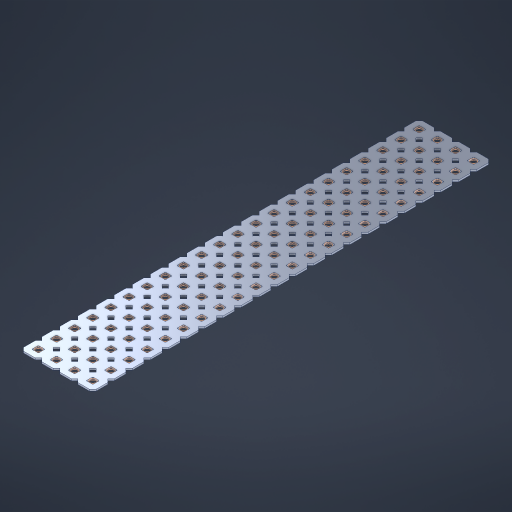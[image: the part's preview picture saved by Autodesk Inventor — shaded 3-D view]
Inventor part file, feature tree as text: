
AUTODESK INVENTOR PART (.ipt)
format: ipt  version: 2023 (Build 270158000, 158)  size: 1,275,392 bytes
history: native  units: in
note: dims shown in document units (in); Inventor stores cm internally (conversion verified against a paired STEP export)
features: other x89, extrude x87, sketch x2, pattern_linear x1
ambient origin geometry x8: Origin, YZ Plane, XZ Plane, XY Plane, X Axis, Y Axis, Z Axis, Center Point
bodies: Solid1 (feature_tree), Body (feature_tree)
feature tree (179):
  pattern_linear  "Rectangular Pattern1"  Spacing1=0.09in  [1 undecoded]
  sketch  "Sketch1"  dims[d1=0.5in]
  sketch  "Sketch2"  dims[d2=0.182in d3=0.09in d4=0.09in d5=0.09in d6=0.09in d7=0.09in d8=0.09in d9=0.09in d10=0.09in d11=0.02in d13=0.0in d14=0.172in d15=0.0625in d16=0.0in d19=0.5in d22=0.5in]
  other  "Srf1"
  other  "Srf126"
  other  "Srf127"
  other  "Srf128"
  other  "Srf129"
  other  "Srf130"
  other  "Srf131"
  other  "Srf250"
  other  "Srf251"
  other  "Srf252"
  other  "Srf253"
  other  "Srf254"
  other  "Srf255"
  other  "Srf256"
  other  "Srf257"
  other  "Srf258"
  other  "Srf259"
  other  "Srf260"
  other  "Srf261"
  other  "Srf262"
  other  "Srf263"
  other  "Srf264"
  other  "Srf268"
  other  "Srf269"
  other  "Srf270"
  other  "Srf271"
  other  "Srf272"
  other  "Srf273"
  other  "Srf274"
  other  "Srf275"
  other  "Srf276"
  other  "Srf277"
  other  "Srf278"
  other  "Srf279"
  other  "Srf280"
  other  "Srf281"
  other  "Srf282"
  other  "Srf283"
  other  "Srf284"
  other  "Srf285"
  other  "Srf286"
  other  "Srf287"
  other  "Srf288"
  other  "Srf289"
  other  "Srf293"
  other  "Srf294"
  other  "Srf295"
  other  "Srf296"
  other  "Srf297"
  other  "Srf298"
  other  "Srf299"
  other  "Srf300"
  other  "Srf301"
  other  "Srf302"
  other  "Srf303"
  other  "Srf304"
  other  "Srf305"
  other  "Srf306"
  other  "Srf307"
  other  "Srf308"
  other  "Srf309"
  other  "Srf310"
  other  "Srf311"
  other  "Srf312"
  other  "Srf313"
  other  "Srf314"
  other  "Srf318"
  other  "Srf319"
  other  "Srf320"
  other  "Srf321"
  other  "Srf322"
  other  "Srf323"
  other  "Srf324"
  other  "Srf325"
  other  "Srf326"
  other  "Srf327"
  other  "Srf328"
  other  "Srf329"
  other  "Srf330"
  other  "Srf331"
  other  "Srf332"
  other  "Srf333"
  other  "Srf334"
  other  "Srf335"
  other  "Srf336"
  other  "Srf337"
  other  "Srf338"
  other  "Srf339"
  other  "Circle"
  extrude  "ExtrusionSrf126"  Depth=0.09in
  extrude  "ExtrusionSrf127"  Depth=0.09in
  extrude  "ExtrusionSrf128"  Depth=0.09in
  extrude  "ExtrusionSrf129"  Depth=0.09in
  extrude  "ExtrusionSrf130"  Depth=0.09in
  extrude  "ExtrusionSrf131"  Depth=0.09in
  extrude  "ExtrusionSrf250"  Depth=0.09in
  extrude  "ExtrusionSrf251"  Depth=0.02in
  extrude  "ExtrusionSrf252"  TaperAngle=0.0deg  [1 undecoded]
  extrude  "ExtrusionSrf253"  Depth=0.5in
  extrude  "ExtrusionSrf254"  Depth=0.5in TaperAngle=0.0deg
  extrude  "ExtrusionSrf255"  Depth=0.5in
  extrude  "ExtrusionSrf256"  Depth=0.5in
  extrude  "ExtrusionSrf257"  [1 undecoded]
  extrude  "ExtrusionSrf258"  [1 undecoded]
  extrude  "ExtrusionSrf259"  [1 undecoded]
  extrude  "ExtrusionSrf260"  [1 undecoded]
  extrude  "ExtrusionSrf261"  [1 undecoded]
  extrude  "ExtrusionSrf262"  [1 undecoded]
  extrude  "ExtrusionSrf263"  [1 undecoded]
  extrude  "ExtrusionSrf264"  [1 undecoded]
  extrude  "ExtrusionSrf268"  [1 undecoded]
  extrude  "ExtrusionSrf269"  [1 undecoded]
  extrude  "ExtrusionSrf270"  [1 undecoded]
  extrude  "ExtrusionSrf271"  [1 undecoded]
  extrude  "ExtrusionSrf272"  [1 undecoded]
  extrude  "ExtrusionSrf273"  [1 undecoded]
  extrude  "ExtrusionSrf274"  [1 undecoded]
  extrude  "ExtrusionSrf275"  [1 undecoded]
  extrude  "ExtrusionSrf276"  [1 undecoded]
  extrude  "ExtrusionSrf277"  [1 undecoded]
  extrude  "ExtrusionSrf278"  [1 undecoded]
  extrude  "ExtrusionSrf279"  [1 undecoded]
  extrude  "ExtrusionSrf280"  [1 undecoded]
  extrude  "ExtrusionSrf281"  [1 undecoded]
  extrude  "ExtrusionSrf282"  [1 undecoded]
  extrude  "ExtrusionSrf283"  [1 undecoded]
  extrude  "ExtrusionSrf284"  [1 undecoded]
  extrude  "ExtrusionSrf285"  [1 undecoded]
  extrude  "ExtrusionSrf286"  [1 undecoded]
  extrude  "ExtrusionSrf287"  [1 undecoded]
  extrude  "ExtrusionSrf288"  [1 undecoded]
  extrude  "ExtrusionSrf289"  [1 undecoded]
  extrude  "ExtrusionSrf293"  [1 undecoded]
  extrude  "ExtrusionSrf294"  [1 undecoded]
  extrude  "ExtrusionSrf295"  [1 undecoded]
  extrude  "ExtrusionSrf296"  [1 undecoded]
  extrude  "ExtrusionSrf297"  [1 undecoded]
  extrude  "ExtrusionSrf298"  [1 undecoded]
  extrude  "ExtrusionSrf299"  [1 undecoded]
  extrude  "ExtrusionSrf300"  [1 undecoded]
  extrude  "ExtrusionSrf301"  [1 undecoded]
  extrude  "ExtrusionSrf302"  [1 undecoded]
  extrude  "ExtrusionSrf303"  [1 undecoded]
  extrude  "ExtrusionSrf304"  [1 undecoded]
  extrude  "ExtrusionSrf305"  [1 undecoded]
  extrude  "ExtrusionSrf306"  [1 undecoded]
  extrude  "ExtrusionSrf307"  [1 undecoded]
  extrude  "ExtrusionSrf308"  [1 undecoded]
  extrude  "ExtrusionSrf309"  [1 undecoded]
  extrude  "ExtrusionSrf310"  [1 undecoded]
  extrude  "ExtrusionSrf311"  [1 undecoded]
  extrude  "ExtrusionSrf312"  [1 undecoded]
  extrude  "ExtrusionSrf313"  [1 undecoded]
  extrude  "ExtrusionSrf314"  [1 undecoded]
  extrude  "ExtrusionSrf318"  [1 undecoded]
  extrude  "ExtrusionSrf319"  [1 undecoded]
  extrude  "ExtrusionSrf320"  [1 undecoded]
  extrude  "ExtrusionSrf321"  [1 undecoded]
  extrude  "ExtrusionSrf322"  [1 undecoded]
  extrude  "ExtrusionSrf323"  [1 undecoded]
  extrude  "ExtrusionSrf324"  [1 undecoded]
  extrude  "ExtrusionSrf325"  [1 undecoded]
  extrude  "ExtrusionSrf326"  [1 undecoded]
  extrude  "ExtrusionSrf327"  [1 undecoded]
  extrude  "ExtrusionSrf328"  [1 undecoded]
  extrude  "ExtrusionSrf329"  [1 undecoded]
  extrude  "ExtrusionSrf330"  [1 undecoded]
  extrude  "ExtrusionSrf331"  [1 undecoded]
  extrude  "ExtrusionSrf332"  [1 undecoded]
  extrude  "ExtrusionSrf333"  [1 undecoded]
  extrude  "ExtrusionSrf334"  [1 undecoded]
  extrude  "ExtrusionSrf335"  [1 undecoded]
  extrude  "ExtrusionSrf336"  [1 undecoded]
  extrude  "ExtrusionSrf337"  [1 undecoded]
  extrude  "ExtrusionSrf338"  [1 undecoded]
  extrude  "ExtrusionSrf339"  [1 undecoded]
note: 76 required parameter values undecoded (feature->parameter linkage not recoverable at this tier; creation-order binding heuristic only, values carry confidence <= 0.55)
